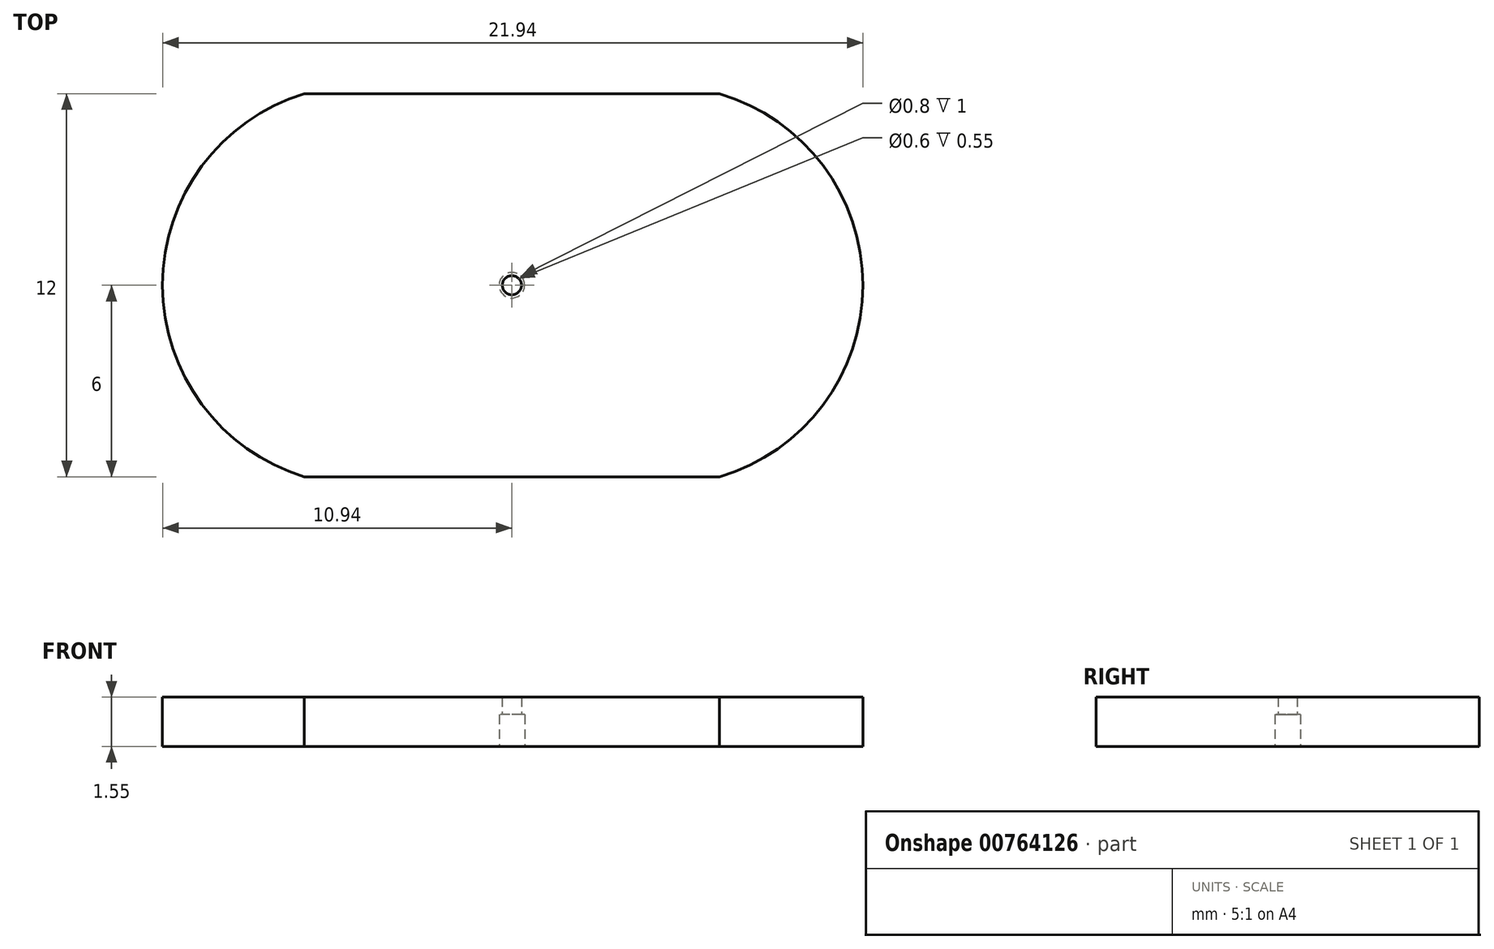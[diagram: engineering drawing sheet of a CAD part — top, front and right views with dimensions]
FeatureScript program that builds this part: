
annotation { "Feature Type Name" : "Feature", "Feature Type Description" : "" }
export const myFeature = defineFeature(function(context is Context, id is Id, definition is map)
    precondition{}
    {
        {
            var Q0;
            Q0=qCreatedBy(makeId("Top.planeOp"),FACE);
            var sketch = newSketch(context, id + "F0", { "sketchPlane" : qUnion([Q0])});
            skLineSegment(sketch, "E0.bottom", {"start": v(6.5, -6) * mm, "end": v(-6.5, -6) * mm});
            skLineSegment(sketch, "E0.top", {"start": v(6.5, 6) * mm, "end": v(-6.5, 6) * mm});
            skPoint(sketch, "E0.middle", {"position": v(0, 0) * mm});
            skLineSegment(sketch, "E1", {"start": v(-11, 7.8) * mm, "end": v(-11, -7.92) * mm, "construction": true});
            skLineSegment(sketch, "E2", {"start": v(11, 7.83) * mm, "end": v(11, -8.37) * mm, "construction": true});
            skArc(sketch, "E3", {"start": v(-6.5, 6) * mm, "mid": v(-10.94, 0) * mm, "end": v(-6.5, -6) * mm});
            skArc(sketch, "E4", {"start": v(6.5, -6) * mm, "mid": v(11, 0) * mm, "end": v(6.5, 6) * mm});
            skCircle(sketch, "E5", {"center": v(0, 0) * mm, "radius": 0.4 * mm});
            skSolve(sketch);
        }
        {
            var Q0;
            Q0=makeQuery(id+"F0.imprint","IMPRINT",FACE,{"disambiguationData":[TD([[makeQuery(id+"F0.imprint","IMPRINT",EDGE,{"derivedFrom":sQuery(id+"F0.wireOp",EDGE,"E0.bottom")}),-1.0]])]});
            extrude(context, id + "F1", {"entities" : qUnion([Q0]), "depth" : 1 * mm, "offsetDistance" : 25 * mm});
        }
        {
            var Q0;
            Q0=makeQuery(id+"F1.opExtrude","CAP_FACE",FACE,{"disambiguationData":[OSD([sQuery(id+"F0.wireOp",EDGE,"E0.bottom"),sQuery(id+"F0.wireOp",EDGE,"E0.top"),sQuery(id+"F0.wireOp",EDGE,"E3"),sQuery(id+"F0.wireOp",EDGE,"E4"),sQuery(id+"F0.wireOp",EDGE,"E5")])],"isStart":false});
            var sketch = newSketch(context, id + "F2", { "sketchPlane" : qUnion([Q0])});
            skArc(sketch, "E6.0", {"start": v(-6.5, 6) * mm, "mid": v(-10.94, 0) * mm, "end": v(-6.5, -6) * mm});
            skLineSegment(sketch, "E6.1", {"start": v(6.5, -6) * mm, "end": v(-6.5, -6) * mm});
            skArc(sketch, "E6.2", {"start": v(6.5, -6) * mm, "mid": v(11, 0) * mm, "end": v(6.5, 6) * mm});
            skLineSegment(sketch, "E6.3", {"start": v(6.5, 6) * mm, "end": v(-6.5, 6) * mm});
            skLineSegment(sketch, "E7.0.3", {"start": v(-6.5, -6) * mm, "end": v(6.5, -6) * mm});
            skCircle(sketch, "E8", {"center": v(0, 0) * mm, "radius": 0.3 * mm});
            skSolve(sketch);
        }
        {
            var Q0;
            Q0 = qSketchRegion(id + "F2", true);
            extrude(context, id + "F3", {"entities" : qUnion([Q0]), "operationType" : NewBodyOperationType.ADD, "depth" : 0.55 * mm, "offsetDistance" : 25 * mm});
        }
    });
